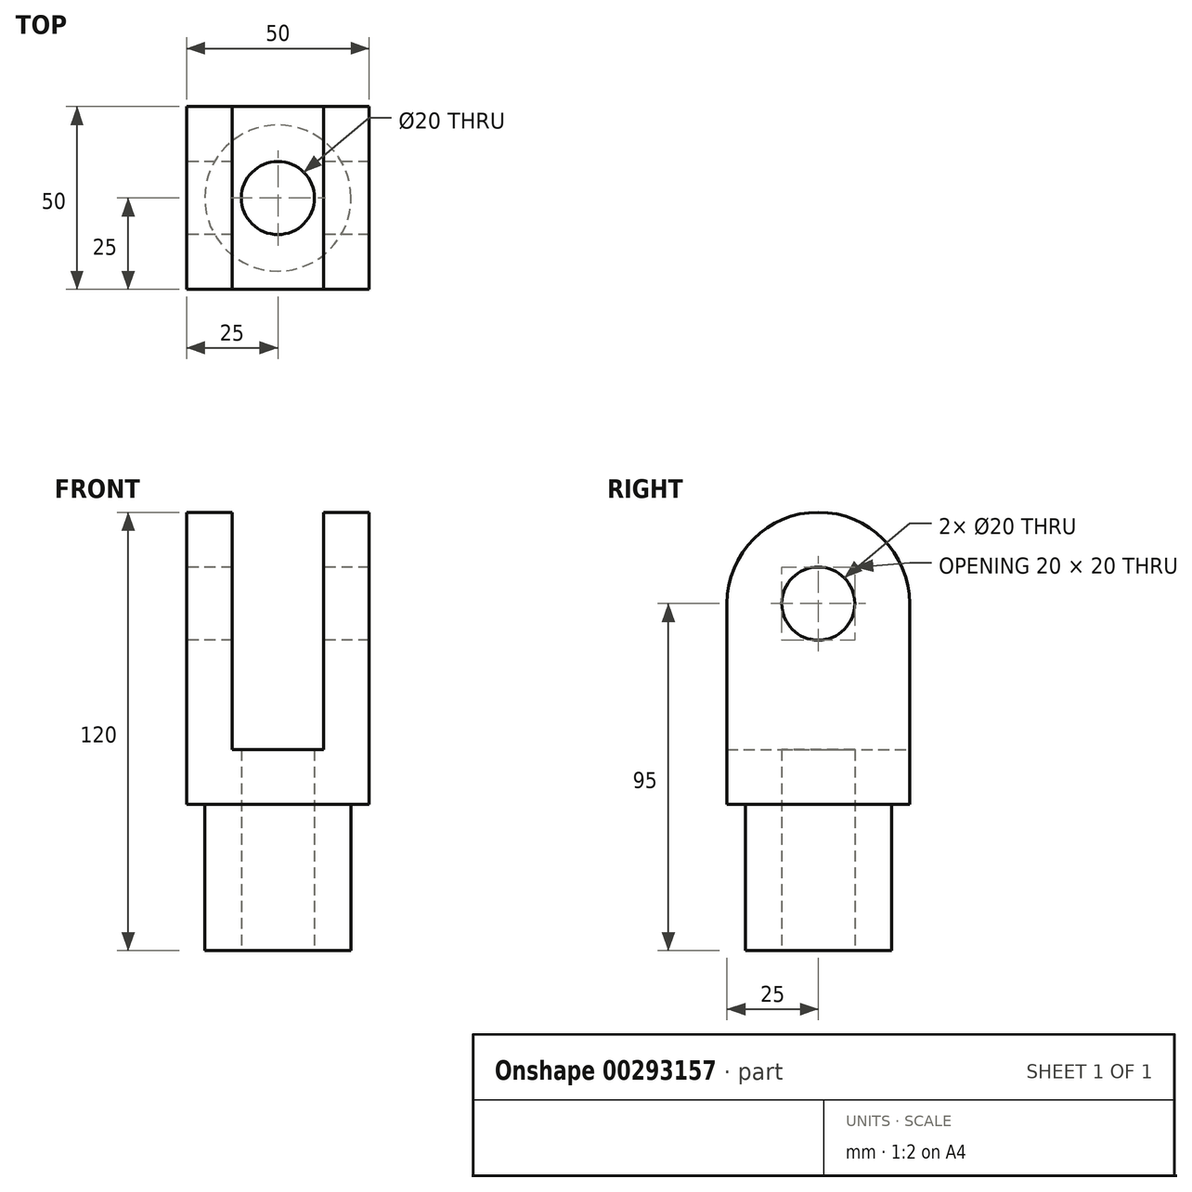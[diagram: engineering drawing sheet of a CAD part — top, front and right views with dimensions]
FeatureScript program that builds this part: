
annotation { "Feature Type Name" : "Feature", "Feature Type Description" : "" }
export const myFeature = defineFeature(function(context is Context, id is Id, definition is map)
    precondition{}
    {
        {
            var Q0;
            Q0=qCreatedBy(makeId("Front.planeOp"),FACE);
            var sketch = newSketch(context, id + "F0", { "sketchPlane" : qUnion([Q0])});
            skLineSegment(sketch, "E0", {"start": v(0, 0) * mm, "end": v(-25, 0) * mm});
            skLineSegment(sketch, "E1", {"start": v(-25, 0) * mm, "end": v(-25, 80) * mm});
            skLineSegment(sketch, "E2", {"start": v(-25, 80) * mm, "end": v(-12.5, 80) * mm});
            skLineSegment(sketch, "E3", {"start": v(-12.5, 80) * mm, "end": v(-12.5, 15) * mm});
            skLineSegment(sketch, "E4", {"start": v(-12.5, 15) * mm, "end": v(0, 15) * mm});
            skLineSegment(sketch, "E5.MirrorCS", {"start": v(0, 0) * mm, "end": v(25, 0) * mm});
            skLineSegment(sketch, "E6.MirrorCS", {"start": v(25, 80) * mm, "end": v(12.5, 80) * mm});
            skLineSegment(sketch, "E7.MirrorCS", {"start": v(12.5, 15) * mm, "end": v(0, 15) * mm});
            skLineSegment(sketch, "E8.MirrorCS", {"start": v(25, 0) * mm, "end": v(25, 80) * mm});
            skLineSegment(sketch, "E9.MirrorCS", {"start": v(12.5, 80) * mm, "end": v(12.5, 15) * mm});
            skSolve(sketch);
        }
        {
            var Q0;
            Q0=makeQuery(id+"F0.imprint","IMPRINT",FACE,{"disambiguationData":[TD([[makeQuery(id+"F0.imprint","IMPRINT",EDGE,{"derivedFrom":sQuery(id+"F0.wireOp",EDGE,"E0")}),-1.0]])]});
            extrude(context, id + "F1", {"entities" : qUnion([Q0]), "depth" : 50 * mm});
        }
        {
            var Q0;
            Q0=makeQuery(id+"F1.opExtrude","SWEPT_FACE",FACE,{"disambiguationData":[OSD([sQuery(id+"F0.wireOp",EDGE,"E1")])]});
            var sketch = newSketch(context, id + "F2", { "sketchPlane" : qUnion([Q0])});
            skCircle(sketch, "E10", {"center": v(25, 55) * mm, "radius": 10 * mm});
            skSolve(sketch);
        }
        {
            var Q0;
            Q0=sQuery(id+"F2.wireOp",VERTEX,"E10.center");
            var Q1;
            Q1=makeQuery(id+"F1.opExtrude","SWEPT_BODY",BODY,{"disambiguationData":[OSD([sQuery(id+"F0.wireOp",EDGE,"E0"),sQuery(id+"F0.wireOp",EDGE,"E1"),sQuery(id+"F0.wireOp",EDGE,"E2"),sQuery(id+"F0.wireOp",EDGE,"E3"),sQuery(id+"F0.wireOp",EDGE,"E4"),sQuery(id+"F0.wireOp",EDGE,"E5.MirrorCS"),sQuery(id+"F0.wireOp",EDGE,"E6.MirrorCS"),sQuery(id+"F0.wireOp",EDGE,"E7.MirrorCS"),sQuery(id+"F0.wireOp",EDGE,"E8.MirrorCS"),sQuery(id+"F0.wireOp",EDGE,"E9.MirrorCS")])]});
            hole(context, id + "F3", {"style" : HoleStyle.SIMPLE, "endStyle" : HoleEndStyle.THROUGH, "holeDiameter" : 20 * mm, "tappedDepth" : 12 * mm, "tapClearance" : 3, "locations" : qUnion([Q0]), "scope" : qUnion([Q1])});
        }
        {
            var Q0;
            Q0=makeQuery(id+"F1.opExtrude","SWEPT_FACE",FACE,{"disambiguationData":[OSD([sQuery(id+"F0.wireOp",EDGE,"E0"),sQuery(id+"F0.wireOp",EDGE,"E5.MirrorCS")])]});
            var sketch = newSketch(context, id + "F4", { "sketchPlane" : qUnion([Q0])});
            skCircle(sketch, "E11", {"center": v(0, 25) * mm, "radius": 20 * mm});
            skSolve(sketch);
        }
        {
            var Q0;
            Q0=makeQuery(id+"F4.imprint","IMPRINT",FACE,{"disambiguationData":[TD([[makeQuery(id+"F4.imprint","IMPRINT",EDGE,{"derivedFrom":sQuery(id+"F4.wireOp",EDGE,"E11")}),1.0]])]});
            extrude(context, id + "F5", {"entities" : qUnion([Q0]), "operationType" : NewBodyOperationType.ADD, "depth" : 40 * mm});
        }
        {
            var Q0;
            Q0=makeQuery(id+"F5.opExtrude","CAP_FACE",FACE,{"disambiguationData":[OSD([sQuery(id+"F4.wireOp",EDGE,"E11")])],"isStart":false});
            var sketch = newSketch(context, id + "F6", { "sketchPlane" : qUnion([Q0])});
            skCircle(sketch, "E12", {"center": v(0, 25) * mm, "radius": 10 * mm});
            skSolve(sketch);
        }
        {
            var Q0;
            Q0=sQuery(id+"F6.wireOp",VERTEX,"E12.center");
            var Q1;
            Q1=makeQuery(id+"F1.opExtrude","SWEPT_BODY",BODY,{"disambiguationData":[OSD([sQuery(id+"F0.wireOp",EDGE,"E0"),sQuery(id+"F0.wireOp",EDGE,"E1"),sQuery(id+"F0.wireOp",EDGE,"E2"),sQuery(id+"F0.wireOp",EDGE,"E3"),sQuery(id+"F0.wireOp",EDGE,"E4"),sQuery(id+"F0.wireOp",EDGE,"E5.MirrorCS"),sQuery(id+"F0.wireOp",EDGE,"E6.MirrorCS"),sQuery(id+"F0.wireOp",EDGE,"E7.MirrorCS"),sQuery(id+"F0.wireOp",EDGE,"E8.MirrorCS"),sQuery(id+"F0.wireOp",EDGE,"E9.MirrorCS")])]});
            hole(context, id + "F7", {"style" : HoleStyle.SIMPLE, "endStyle" : HoleEndStyle.THROUGH, "holeDiameter" : 20 * mm, "tappedDepth" : 12 * mm, "tapClearance" : 3, "locations" : qUnion([Q0]), "scope" : qUnion([Q1])});
        }
        {
            var Q0;
            Q0=makeQuery(id+"F1.opExtrude","CAP_EDGE",EDGE,{"disambiguationData":[OSD([sQuery(id+"F0.wireOp",EDGE,"E6.MirrorCS")])],"isStart":false});
            var Q1;
            Q1=makeQuery(id+"F1.opExtrude","CAP_EDGE",EDGE,{"disambiguationData":[OSD([sQuery(id+"F0.wireOp",EDGE,"E6.MirrorCS")])],"isStart":true});
            var Q2;
            Q2=makeQuery(id+"F1.opExtrude","CAP_EDGE",EDGE,{"disambiguationData":[OSD([sQuery(id+"F0.wireOp",EDGE,"E2")])],"isStart":false});
            var Q3;
            Q3=makeQuery(id+"F1.opExtrude","CAP_EDGE",EDGE,{"disambiguationData":[OSD([sQuery(id+"F0.wireOp",EDGE,"E2")])],"isStart":true});
            fillet(context, id + "F8", {"entities" : qUnion([Q0, Q1, Q2, Q3]), "radius" : 25 * mm, "tangentPropagation" : true, "allowEdgeOverflow" : false});
        }
    });
